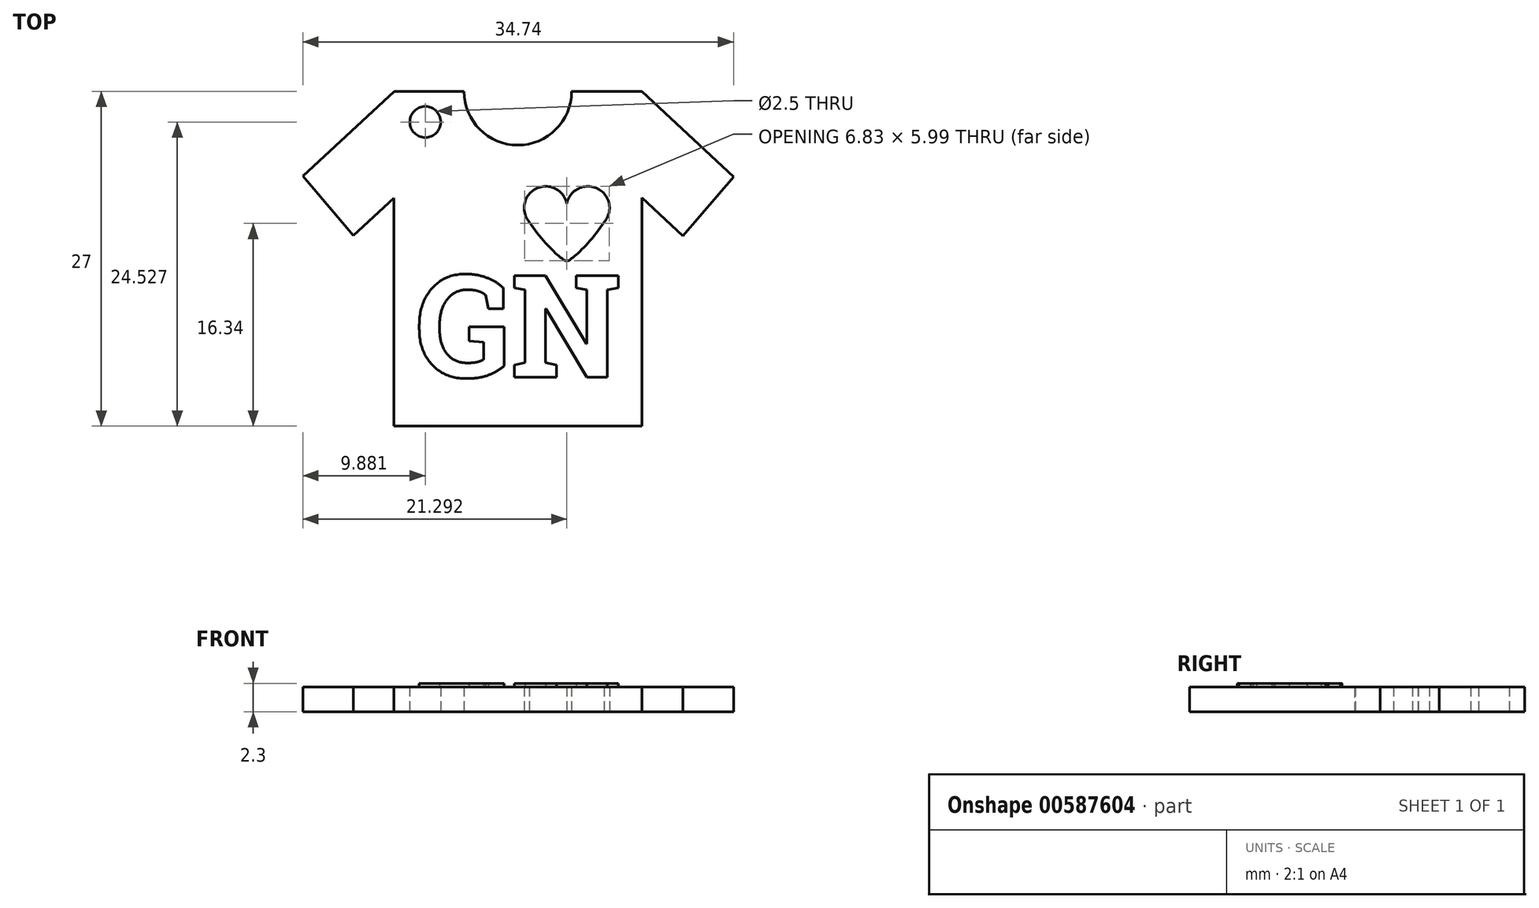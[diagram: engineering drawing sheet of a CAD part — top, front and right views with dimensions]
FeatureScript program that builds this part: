
annotation { "Feature Type Name" : "Feature", "Feature Type Description" : "" }
export const myFeature = defineFeature(function(context is Context, id is Id, definition is map)
    precondition{}
    {
        {
            var Q0;
            Q0=qCreatedBy(makeId("Top.planeOp"),FACE);
            var sketch = newSketch(context, id + "F0", { "sketchPlane" : qUnion([Q0])});
            skLineSegment(sketch, "E0.bottom", {"start": v(-37.63, 30.13) * mm, "end": v(-17.63, 30.13) * mm});
            skLineSegment(sketch, "E0.top", {"start": v(-37.63, 3.13) * mm, "end": v(-17.63, 3.13) * mm});
            skLineSegment(sketch, "E0.left", {"start": v(-37.63, 30.13) * mm, "end": v(-37.63, 3.13) * mm});
            skLineSegment(sketch, "E0.right", {"start": v(-17.63, 30.13) * mm, "end": v(-17.63, 3.13) * mm});
            skLineSegment(sketch, "E1", {"start": v(-17.63, 30.13) * mm, "end": v(-10.23, 23.23) * mm});
            skLineSegment(sketch, "E2", {"start": v(-17.63, 21.55) * mm, "end": v(-14.33, 18.47) * mm});
            skLineSegment(sketch, "E3", {"start": v(-14.33, 18.47) * mm, "end": v(-10.23, 23.23) * mm});
            skPoint(sketch, "E4.endSnap0", {"position": v(-27.63, 3.13) * mm});
            skLineSegment(sketch, "E5", {"start": v(-27.63, 3.13) * mm, "end": v(-27.58, 40.3) * mm, "construction": true});
            skPoint(sketch, "E6", {"position": v(-27.63, 30.13) * mm});
            skArc(sketch, "E7", {"start": v(-31.96, 30.13) * mm, "mid": v(-27.63, 25.79) * mm, "end": v(-23.29, 30.13) * mm});
            skLineSegment(sketch, "E8.MirrorCS", {"start": v(-37.58, 21.57) * mm, "end": v(-40.88, 18.51) * mm});
            skLineSegment(sketch, "E9.MirrorCS", {"start": v(-40.88, 18.51) * mm, "end": v(-44.97, 23.28) * mm});
            skLineSegment(sketch, "E10.MirrorCS", {"start": v(-37.55, 30.15) * mm, "end": v(-44.97, 23.28) * mm});
            skCircle(sketch, "E11", {"center": v(-35.09, 27.66) * mm, "radius": 1.25 * mm});
            skCircle(sketch, "E12", {"center": v(-21.97, 20.73) * mm, "radius": 1.74 * mm});
            skLineSegment(sketch, "E13", {"start": v(-23.68, 21.07) * mm, "end": v(-23.68, 16.48) * mm, "construction": true});
            skFitSpline(sketch, "E14", {"points": [v(-20.34, 20.13) * mm, v(-23.68, 16.48) * mm, v(-23.55, 17.74) * mm], "startDerivative": vector(-4.56, -8.42) * mm, "endDerivative": vector(-2.39, 3.68) * mm});
            skFitSpline(sketch, "E15.MirrorCS", {"points": [v(-27.02, 20.13) * mm, v(-23.68, 16.48) * mm, v(-23.81, 17.74) * mm], "startDerivative": vector(4.56, -8.42) * mm, "endDerivative": vector(2.39, 3.68) * mm});
            skCircle(sketch, "E16.MirrorC", {"center": v(-25.38, 20.73) * mm, "radius": 1.74 * mm});
            skSolve(sketch);
        }
        {
            var Q0;
            {var subQ4=sQuery(id+"F0.wireOp",EDGE,"E0.top");Q0=makeQuery(id+"F0.imprint","IMPRINT",FACE,{"disambiguationData":[TD([[makeQuery(id+"F0.imprint","IMPRINT",EDGE,{"derivedFrom":subQ4}),1.0]])]});}
            var Q1;
            {var subQ2=sQuery(id+"F0.wireOp",EDGE,"E8.MirrorCS");Q1=makeQuery(id+"F0.imprint","IMPRINT",FACE,{"disambiguationData":[TD([[makeQuery(id+"F0.imprint","IMPRINT",EDGE,{"derivedFrom":subQ2}),-1.0]])]});}
            var Q2;
            {var subQ0=sQuery(id+"F0.wireOp",EDGE,"E1");Q2=makeQuery(id+"F0.imprint","IMPRINT",FACE,{"disambiguationData":[TD([[makeQuery(id+"F0.imprint","IMPRINT",EDGE,{"derivedFrom":subQ0}),-1.0]])]});}
            extrude(context, id + "F1", {"entities" : qUnion([Q0, Q1, Q2]), "depth" : 2 * mm, "offsetDistance" : 25 * mm});
        }
        {
            var Q0;
            Q0=makeQuery(id+"F1.opExtrude","CAP_FACE",FACE,{"disambiguationData":[OSD([sQuery(id+"F0.wireOp",EDGE,"E0.bottom"),sQuery(id+"F0.wireOp",EDGE,"E0.top"),sQuery(id+"F0.wireOp",EDGE,"E0.left"),sQuery(id+"F0.wireOp",EDGE,"E0.right"),sQuery(id+"F0.wireOp",EDGE,"E1"),sQuery(id+"F0.wireOp",EDGE,"E2"),sQuery(id+"F0.wireOp",EDGE,"E3"),sQuery(id+"F0.wireOp",EDGE,"E7"),sQuery(id+"F0.wireOp",EDGE,"E8.MirrorCS"),sQuery(id+"F0.wireOp",EDGE,"E9.MirrorCS"),sQuery(id+"F0.wireOp",EDGE,"E10.MirrorCS"),sQuery(id+"F0.wireOp",EDGE,"E11"),sQuery(id+"F0.wireOp",EDGE,"E12"),sQuery(id+"F0.wireOp",EDGE,"E14"),sQuery(id+"F0.wireOp",EDGE,"E15.MirrorCS"),sQuery(id+"F0.wireOp",EDGE,"E16.MirrorC")])],"isStart":false});
            var sketch = newSketch(context, id + "F2", { "sketchPlane" : qUnion([Q0])});
            skText(sketch, "E17", { "text": "GN", "fontName": "RobotoSlab-Bold.ttf"});
            const initialGuessF2  = {"E17": [-0.03584, 0.00708, 1, 0, 0.0083]};
            skSetInitialGuess(sketch, initialGuessF2);
            skSolve(sketch);
        }
        {
            var Q0;
            Q0 = qSketchRegion(id + "F2", true);
            extrude(context, id + "F3", {"entities" : qUnion([Q0]), "operationType" : NewBodyOperationType.ADD, "depth" : 0.3 * mm, "offsetDistance" : 25 * mm});
        }
    });
